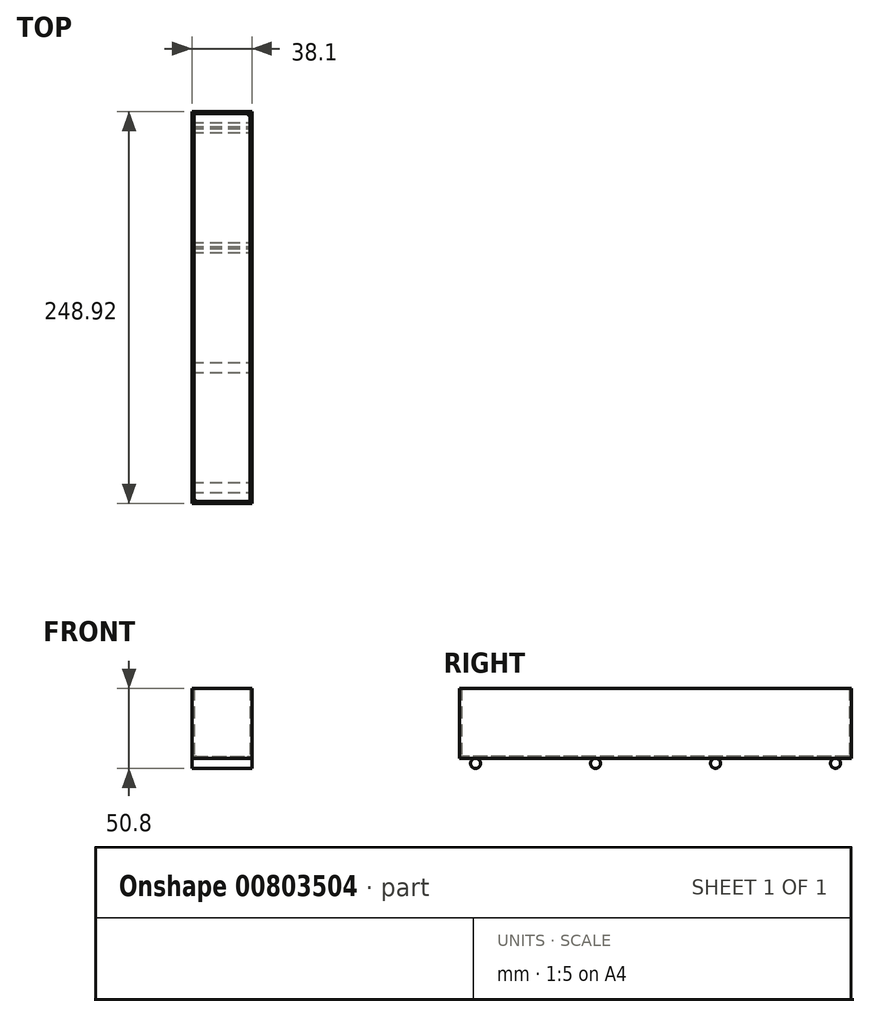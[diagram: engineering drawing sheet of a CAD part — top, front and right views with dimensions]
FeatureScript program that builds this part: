
annotation { "Feature Type Name" : "Feature", "Feature Type Description" : "" }
export const myFeature = defineFeature(function(context is Context, id is Id, definition is map)
    precondition{}
    {
        {
            var Q0;
            Q0=qCreatedBy(makeId("Top.planeOp"),FACE);
            var sketch = newSketch(context, id + "F0", { "sketchPlane" : qUnion([Q0])});
            skLineSegment(sketch, "E0.bottom", {"start": v(-19.05, 124.46) * mm, "end": v(19.05, 124.46) * mm});
            skLineSegment(sketch, "E0.top", {"start": v(-19.05, -124.46) * mm, "end": v(19.05, -124.46) * mm});
            skLineSegment(sketch, "E0.left", {"start": v(-19.05, 124.46) * mm, "end": v(-19.05, -124.46) * mm});
            skLineSegment(sketch, "E0.right", {"start": v(19.05, 124.46) * mm, "end": v(19.05, -124.46) * mm});
            skCircle(sketch, "E1", {"center": v(-19.05, 124.46) * mm, "radius": 3.18 * mm});
            skCircle(sketch, "E2", {"center": v(-19.05, 124.46) * mm, "radius": 2.92 * mm});
            skLineSegment(sketch, "E3", {"start": v(0, 124.46) * mm, "end": v(0, -124.46) * mm, "construction": true});
            skLineSegment(sketch, "E4", {"start": v(-19.05, 0) * mm, "end": v(19.05, 0) * mm, "construction": true});
            skCircle(sketch, "E5.MirrorC", {"center": v(19.05, 124.46) * mm, "radius": 3.18 * mm});
            skCircle(sketch, "E6.MirrorC", {"center": v(19.05, 124.46) * mm, "radius": 2.92 * mm});
            skCircle(sketch, "E7.MirrorC", {"center": v(-19.05, -124.46) * mm, "radius": 3.18 * mm});
            skCircle(sketch, "E8.MirrorC", {"center": v(-19.05, -124.46) * mm, "radius": 2.92 * mm});
            skCircle(sketch, "E9.MirrorC", {"center": v(19.05, -124.46) * mm, "radius": 3.18 * mm});
            skCircle(sketch, "E10.MirrorC", {"center": v(19.05, -124.46) * mm, "radius": 2.92 * mm});
            skLineSegment(sketch, "E11.bottom", {"start": v(-17.78, 123.2) * mm, "end": v(17.78, 123.2) * mm});
            skLineSegment(sketch, "E11.top", {"start": v(-17.78, -123.2) * mm, "end": v(17.78, -123.2) * mm});
            skLineSegment(sketch, "E11.left", {"start": v(-17.78, 123.2) * mm, "end": v(-17.78, -123.2) * mm});
            skLineSegment(sketch, "E11.right", {"start": v(17.78, 123.2) * mm, "end": v(17.78, -123.2) * mm});
            skSolve(sketch);
        }
        {
            var Q0;
            Q0=makeQuery(id+"F0.imprint","IMPRINT",FACE,{"disambiguationData":[TD([[makeQuery(id+"F0.imprint","IMPRINT",EDGE,{"derivedFrom":sQuery(id+"F0.wireOp",EDGE,"E0.bottom")}),-1.0]])]});
            var Q1;
            {var subQ5=sQuery(id+"F0.wireOp",EDGE,"E1");var subQ13=sQuery(id+"F0.wireOp",EDGE,"E0.bottom");var subQ14=makeQuery(id+"F0.imprint","INTERSECT",VERTEX,{"derivedFrom":[subQ13,subQ5]});Q1=makeQuery(id+"F0.imprint","IMPRINT",FACE,{"disambiguationData":[TD([[makeQuery(id+"F0.imprint","IMPRINT",EDGE,{"disambiguationData":[TD([[subQ14,-1.0]])],"derivedFrom":subQ13}),-1.0]])]});}
            var Q2;
            {var subQ0=sQuery(id+"F0.wireOp",EDGE,"E0.left");var subQ1=sQuery(id+"F0.wireOp",EDGE,"E0.top");var subQ2=makeQuery(id+"F0.imprint","INTERSECT",VERTEX,{"derivedFrom":[subQ1,subQ0]});Q2=makeQuery(id+"F0.imprint","IMPRINT",FACE,{"disambiguationData":[TD([[makeQuery(id+"F0.imprint","IMPRINT",EDGE,{"disambiguationData":[TD([[subQ2,-1.0]])],"derivedFrom":subQ1}),1.0]])]});}
            var Q3;
            {var subQ0=sQuery(id+"F0.wireOp",EDGE,"E0.right");var subQ1=sQuery(id+"F0.wireOp",EDGE,"E0.top");var subQ2=makeQuery(id+"F0.imprint","INTERSECT",VERTEX,{"derivedFrom":[subQ1,subQ0]});Q3=makeQuery(id+"F0.imprint","IMPRINT",FACE,{"disambiguationData":[TD([[makeQuery(id+"F0.imprint","IMPRINT",EDGE,{"disambiguationData":[TD([[subQ2,1.0]])],"derivedFrom":subQ1}),1.0]])]});}
            var Q4;
            {var subQ0=sQuery(id+"F0.wireOp",EDGE,"E9.MirrorC");var subQ1=sQuery(id+"F0.wireOp",EDGE,"E0.top");var subQ2=makeQuery(id+"F0.imprint","INTERSECT",VERTEX,{"derivedFrom":[subQ1,subQ0]});Q4=makeQuery(id+"F0.imprint","IMPRINT",FACE,{"disambiguationData":[TD([[makeQuery(id+"F0.imprint","IMPRINT",EDGE,{"disambiguationData":[TD([[subQ2,-1.0]])],"derivedFrom":subQ1}),1.0]])]});}
            var Q5;
            {var subQ0=sQuery(id+"F0.wireOp",EDGE,"E1");var subQ1=sQuery(id+"F0.wireOp",EDGE,"E0.left");var subQ2=makeQuery(id+"F0.imprint","INTERSECT",VERTEX,{"derivedFrom":[subQ1,subQ0]});Q5=makeQuery(id+"F0.imprint","IMPRINT",FACE,{"disambiguationData":[TD([[makeQuery(id+"F0.imprint","IMPRINT",EDGE,{"disambiguationData":[TD([[subQ2,-1.0]])],"derivedFrom":subQ1}),1.0]])]});}
            var Q6;
            {var subQ1=sQuery(id+"F0.wireOp",EDGE,"E0.bottom");var subQ5=sQuery(id+"F0.wireOp",EDGE,"E0.left");var subQ9=makeQuery(id+"F0.imprint","INTERSECT",VERTEX,{"derivedFrom":[subQ1,subQ5]});Q6=makeQuery(id+"F0.imprint","IMPRINT",FACE,{"disambiguationData":[TD([[makeQuery(id+"F0.imprint","IMPRINT",EDGE,{"disambiguationData":[TD([[subQ9,-1.0]])],"derivedFrom":subQ1}),-1.0]])]});}
            var Q7;
            {var subQ0=sQuery(id+"F0.wireOp",EDGE,"E5.MirrorC");var subQ1=sQuery(id+"F0.wireOp",EDGE,"E0.right");var subQ2=makeQuery(id+"F0.imprint","INTERSECT",VERTEX,{"derivedFrom":[subQ1,subQ0]});Q7=makeQuery(id+"F0.imprint","IMPRINT",FACE,{"disambiguationData":[TD([[makeQuery(id+"F0.imprint","IMPRINT",EDGE,{"disambiguationData":[TD([[subQ2,-1.0]])],"derivedFrom":subQ1}),-1.0]])]});}
            var Q8;
            {var subQ1=sQuery(id+"F0.wireOp",EDGE,"E0.right");var subQ5=sQuery(id+"F0.wireOp",EDGE,"E0.bottom");var subQ9=makeQuery(id+"F0.imprint","INTERSECT",VERTEX,{"derivedFrom":[subQ5,subQ1]});Q8=makeQuery(id+"F0.imprint","IMPRINT",FACE,{"disambiguationData":[TD([[makeQuery(id+"F0.imprint","IMPRINT",EDGE,{"disambiguationData":[TD([[subQ9,1.0]])],"derivedFrom":subQ5}),-1.0]])]});}
            var Q9;
            {var subQ0=sQuery(id+"F0.wireOp",EDGE,"E7.MirrorC");var subQ1=sQuery(id+"F0.wireOp",EDGE,"E0.top");var subQ2=makeQuery(id+"F0.imprint","INTERSECT",VERTEX,{"derivedFrom":[subQ1,subQ0]});Q9=makeQuery(id+"F0.imprint","IMPRINT",FACE,{"disambiguationData":[TD([[makeQuery(id+"F0.imprint","IMPRINT",EDGE,{"disambiguationData":[TD([[subQ2,-1.0]])],"derivedFrom":subQ1}),1.0]])]});}
            var Q10;
            {var subQ0=sQuery(id+"F0.wireOp",EDGE,"E9.MirrorC");var subQ1=sQuery(id+"F0.wireOp",EDGE,"E0.right");var subQ2=makeQuery(id+"F0.imprint","INTERSECT",VERTEX,{"derivedFrom":[subQ1,subQ0]});Q10=makeQuery(id+"F0.imprint","IMPRINT",FACE,{"disambiguationData":[TD([[makeQuery(id+"F0.imprint","IMPRINT",EDGE,{"disambiguationData":[TD([[subQ2,-1.0]])],"derivedFrom":subQ1}),-1.0]])]});}
            var Q11;
            {var subQ0=sQuery(id+"F0.wireOp",EDGE,"E7.MirrorC");var subQ1=sQuery(id+"F0.wireOp",EDGE,"E0.top");var subQ2=makeQuery(id+"F0.imprint","INTERSECT",VERTEX,{"derivedFrom":[subQ1,subQ0]});Q11=makeQuery(id+"F0.imprint","IMPRINT",FACE,{"disambiguationData":[TD([[makeQuery(id+"F0.imprint","IMPRINT",EDGE,{"disambiguationData":[TD([[subQ2,1.0]])],"derivedFrom":subQ1}),1.0]])]});}
            var Q12;
            {var subQ0=sQuery(id+"F0.wireOp",EDGE,"E7.MirrorC");var subQ1=sQuery(id+"F0.wireOp",EDGE,"E0.left");var subQ2=makeQuery(id+"F0.imprint","INTERSECT",VERTEX,{"derivedFrom":[subQ1,subQ0]});Q12=makeQuery(id+"F0.imprint","IMPRINT",FACE,{"disambiguationData":[TD([[makeQuery(id+"F0.imprint","IMPRINT",EDGE,{"disambiguationData":[TD([[subQ2,-1.0]])],"derivedFrom":subQ1}),1.0]])]});}
            var Q13;
            {var subQ0=sQuery(id+"F0.wireOp",EDGE,"E5.MirrorC");var subQ1=sQuery(id+"F0.wireOp",EDGE,"E0.right");var subQ2=makeQuery(id+"F0.imprint","INTERSECT",VERTEX,{"derivedFrom":[subQ1,subQ0]});Q13=makeQuery(id+"F0.imprint","IMPRINT",FACE,{"disambiguationData":[TD([[makeQuery(id+"F0.imprint","IMPRINT",EDGE,{"disambiguationData":[TD([[subQ2,1.0]])],"derivedFrom":subQ1}),-1.0]])]});}
            var Q14;
            {var subQ0=sQuery(id+"F0.wireOp",EDGE,"E1");var subQ1=sQuery(id+"F0.wireOp",EDGE,"E0.left");var subQ2=makeQuery(id+"F0.imprint","INTERSECT",VERTEX,{"derivedFrom":[subQ1,subQ0]});Q14=makeQuery(id+"F0.imprint","IMPRINT",FACE,{"disambiguationData":[TD([[makeQuery(id+"F0.imprint","IMPRINT",EDGE,{"disambiguationData":[TD([[subQ2,1.0]])],"derivedFrom":subQ1}),1.0]])]});}
            extrude(context, id + "F1", {"entities" : qUnion([Q0, Q1, Q2, Q3, Q4, Q5, Q6, Q7, Q8, Q9, Q10, Q11, Q12, Q13, Q14]), "depth" : 44.45 * mm, "offsetDistance" : 25.4 * mm});
        }
        {
            var Q0;
            {var subQ5=sQuery(id+"F0.wireOp",EDGE,"E11.left");var subQ13=sQuery(id+"F0.wireOp",EDGE,"E1");var subQ14=makeQuery(id+"F0.imprint","INTERSECT",VERTEX,{"derivedFrom":[subQ13,subQ5]});Q0=makeQuery(id+"F0.imprint","IMPRINT",FACE,{"disambiguationData":[TD([[makeQuery(id+"F0.imprint","IMPRINT",EDGE,{"disambiguationData":[TD([[subQ14,-1.0]])],"derivedFrom":subQ13}),-1.0]])]});}
            var Q1;
            {var subQ0=sQuery(id+"F0.wireOp",EDGE,"E11.left");var subQ1=sQuery(id+"F0.wireOp",EDGE,"E2");var subQ2=makeQuery(id+"F0.imprint","INTERSECT",VERTEX,{"derivedFrom":[subQ1,subQ0]});Q1=makeQuery(id+"F0.imprint","IMPRINT",FACE,{"disambiguationData":[TD([[makeQuery(id+"F0.imprint","IMPRINT",EDGE,{"disambiguationData":[TD([[subQ2,-1.0]])],"derivedFrom":subQ1}),1.0]])]});}
            var Q2;
            {var subQ0=sQuery(id+"F0.wireOp",EDGE,"E11.left");var subQ1=sQuery(id+"F0.wireOp",EDGE,"E1");var subQ2=makeQuery(id+"F0.imprint","INTERSECT",VERTEX,{"derivedFrom":[subQ1,subQ0]});Q2=makeQuery(id+"F0.imprint","IMPRINT",FACE,{"disambiguationData":[TD([[makeQuery(id+"F0.imprint","IMPRINT",EDGE,{"disambiguationData":[TD([[subQ2,-1.0]])],"derivedFrom":subQ1}),1.0]])]});}
            var Q3;
            {var subQ0=sQuery(id+"F0.wireOp",EDGE,"E11.right");var subQ1=sQuery(id+"F0.wireOp",EDGE,"E6.MirrorC");var subQ2=makeQuery(id+"F0.imprint","INTERSECT",VERTEX,{"derivedFrom":[subQ1,subQ0]});Q3=makeQuery(id+"F0.imprint","IMPRINT",FACE,{"disambiguationData":[TD([[makeQuery(id+"F0.imprint","IMPRINT",EDGE,{"disambiguationData":[TD([[subQ2,-1.0]])],"derivedFrom":subQ1}),-1.0]])]});}
            var Q4;
            {var subQ0=sQuery(id+"F0.wireOp",EDGE,"E11.right");var subQ1=sQuery(id+"F0.wireOp",EDGE,"E5.MirrorC");var subQ2=makeQuery(id+"F0.imprint","INTERSECT",VERTEX,{"derivedFrom":[subQ1,subQ0]});Q4=makeQuery(id+"F0.imprint","IMPRINT",FACE,{"disambiguationData":[TD([[makeQuery(id+"F0.imprint","IMPRINT",EDGE,{"disambiguationData":[TD([[subQ2,-1.0]])],"derivedFrom":subQ1}),-1.0]])]});}
            var Q5;
            {var subQ0=sQuery(id+"F0.wireOp",EDGE,"E11.right");var subQ1=sQuery(id+"F0.wireOp",EDGE,"E10.MirrorC");var subQ2=makeQuery(id+"F0.imprint","INTERSECT",VERTEX,{"derivedFrom":[subQ1,subQ0]});Q5=makeQuery(id+"F0.imprint","IMPRINT",FACE,{"disambiguationData":[TD([[makeQuery(id+"F0.imprint","IMPRINT",EDGE,{"disambiguationData":[TD([[subQ2,-1.0]])],"derivedFrom":subQ1}),1.0]])]});}
            var Q6;
            {var subQ0=sQuery(id+"F0.wireOp",EDGE,"E11.right");var subQ1=sQuery(id+"F0.wireOp",EDGE,"E9.MirrorC");var subQ2=makeQuery(id+"F0.imprint","INTERSECT",VERTEX,{"derivedFrom":[subQ1,subQ0]});Q6=makeQuery(id+"F0.imprint","IMPRINT",FACE,{"disambiguationData":[TD([[makeQuery(id+"F0.imprint","IMPRINT",EDGE,{"disambiguationData":[TD([[subQ2,-1.0]])],"derivedFrom":subQ1}),1.0]])]});}
            var Q7;
            {var subQ0=sQuery(id+"F0.wireOp",EDGE,"E11.left");var subQ1=sQuery(id+"F0.wireOp",EDGE,"E7.MirrorC");var subQ2=makeQuery(id+"F0.imprint","INTERSECT",VERTEX,{"derivedFrom":[subQ1,subQ0]});Q7=makeQuery(id+"F0.imprint","IMPRINT",FACE,{"disambiguationData":[TD([[makeQuery(id+"F0.imprint","IMPRINT",EDGE,{"disambiguationData":[TD([[subQ2,-1.0]])],"derivedFrom":subQ1}),-1.0]])]});}
            var Q8;
            {var subQ0=sQuery(id+"F0.wireOp",EDGE,"E11.left");var subQ1=sQuery(id+"F0.wireOp",EDGE,"E8.MirrorC");var subQ2=makeQuery(id+"F0.imprint","INTERSECT",VERTEX,{"derivedFrom":[subQ1,subQ0]});Q8=makeQuery(id+"F0.imprint","IMPRINT",FACE,{"disambiguationData":[TD([[makeQuery(id+"F0.imprint","IMPRINT",EDGE,{"disambiguationData":[TD([[subQ2,-1.0]])],"derivedFrom":subQ1}),-1.0]])]});}
            extrude(context, id + "F2", {"entities" : qUnion([Q0, Q1, Q2, Q3, Q4, Q5, Q6, Q7, Q8]), "operationType" : NewBodyOperationType.ADD, "depth" : 1.27 * mm, "offsetDistance" : 25.4 * mm});
        }
        {
            var Q0;
            Q0=makeQuery(id+"F1.opExtrude","SWEPT_FACE",FACE,{"disambiguationData":[OSD([sQuery(id+"F0.wireOp",EDGE,"E0.right")])]});
            var sketch = newSketch(context, id + "F3", { "sketchPlane" : qUnion([Q0])});
            skCircle(sketch, "E12", {"center": v(-114.3, -3.18) * mm, "radius": 3.18 * mm});
            skCircle(sketch, "E13", {"center": v(-38.1, -3.17) * mm, "radius": 3.18 * mm});
            skCircle(sketch, "E14", {"center": v(38.1, -3.1) * mm, "radius": 3.18 * mm});
            skCircle(sketch, "E15", {"center": v(114.3, -3.1) * mm, "radius": 3.18 * mm});
            skSolve(sketch);
        }
        {
            var Q0;
            Q0=makeQuery(id+"F3.imprint","IMPRINT",FACE,{"disambiguationData":[TD([[makeQuery(id+"F3.imprint","IMPRINT",EDGE,{"derivedFrom":sQuery(id+"F3.wireOp",EDGE,"E12")}),1.0]])]});
            var Q1;
            Q1=makeQuery(id+"F3.imprint","IMPRINT",FACE,{"disambiguationData":[TD([[makeQuery(id+"F3.imprint","IMPRINT",EDGE,{"derivedFrom":sQuery(id+"F3.wireOp",EDGE,"E13")}),1.0]])]});
            var Q2;
            {var subQ0=sQuery(id+"F3.wireOp",EDGE,"E14");var subQ1=makeQuery(id+"F1.opExtrude","CAP_EDGE",EDGE,{"disambiguationData":[OSD([sQuery(id+"F0.wireOp",EDGE,"E0.right")])],"isStart":true});var subQ2=makeQuery(id+"F3.imprint","INTERSECT",VERTEX,{"disambiguationData":[OD(0.0)],"derivedFrom":[subQ1,subQ0]});Q2=makeQuery(id+"F3.imprint","IMPRINT",FACE,{"disambiguationData":[TD([[makeQuery(id+"F3.imprint","IMPRINT",EDGE,{"disambiguationData":[TD([[subQ2,-1.0]])],"derivedFrom":subQ0}),1.0]])]});}
            var Q3;
            {var subQ0=sQuery(id+"F3.wireOp",EDGE,"E15");var subQ1=makeQuery(id+"F1.opExtrude","CAP_EDGE",EDGE,{"disambiguationData":[OSD([sQuery(id+"F0.wireOp",EDGE,"E0.right")])],"isStart":true});var subQ2=makeQuery(id+"F3.imprint","INTERSECT",VERTEX,{"disambiguationData":[OD(0.0)],"derivedFrom":[subQ1,subQ0]});Q3=makeQuery(id+"F3.imprint","IMPRINT",FACE,{"disambiguationData":[TD([[makeQuery(id+"F3.imprint","IMPRINT",EDGE,{"disambiguationData":[TD([[subQ2,1.0]])],"derivedFrom":subQ0}),1.0]])]});}
            extrude(context, id + "F4", {"entities" : qUnion([Q0, Q1, Q2, Q3]), "oppositeDirection" : true, "depth" : 38.1 * mm, "offsetDistance" : 25.4 * mm});
        }
    });
